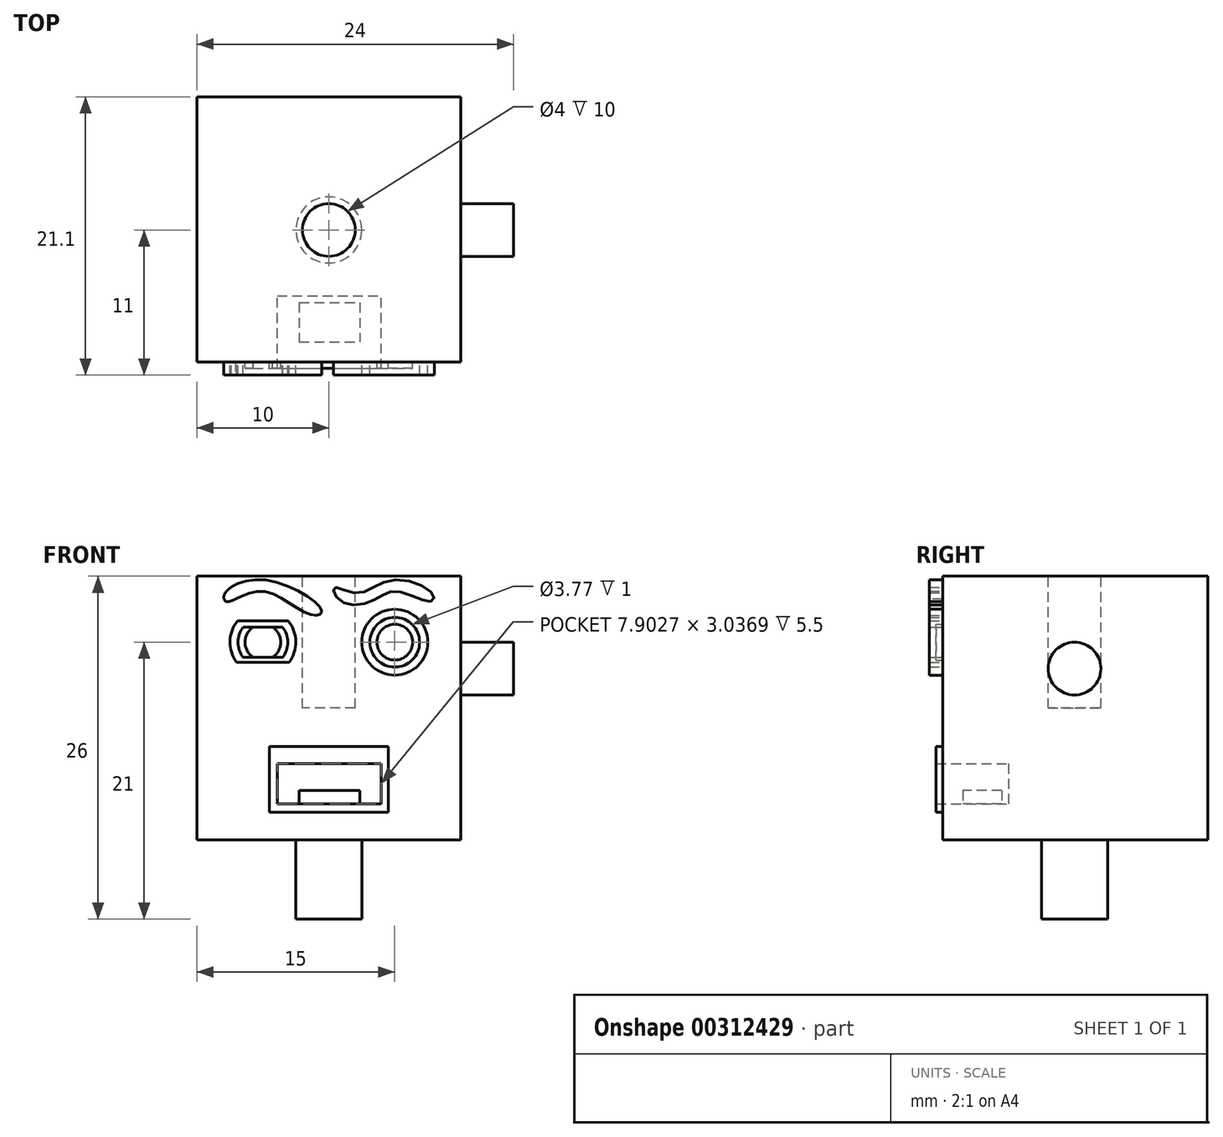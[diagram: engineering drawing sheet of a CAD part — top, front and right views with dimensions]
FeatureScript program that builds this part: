
annotation { "Feature Type Name" : "Feature", "Feature Type Description" : "" }
export const myFeature = defineFeature(function(context is Context, id is Id, definition is map)
    precondition{}
    {
        {
            var Q0;
            Q0=qCreatedBy(makeId("Front.planeOp"),FACE);
            var sketch = newSketch(context, id + "F0", { "sketchPlane" : qUnion([Q0])});
            skLineSegment(sketch, "E0.bottom", {"start": v(-10, 10) * mm, "end": v(10, 10) * mm});
            skLineSegment(sketch, "E0.top", {"start": v(-10, -10) * mm, "end": v(10, -10) * mm});
            skLineSegment(sketch, "E0.left", {"start": v(-10, 10) * mm, "end": v(-10, -10) * mm});
            skLineSegment(sketch, "E0.right", {"start": v(10, 10) * mm, "end": v(10, -10) * mm});
            skLineSegment(sketch, "E1", {"start": v(0, 10) * mm, "end": v(0, -10) * mm, "construction": true});
            skSolve(sketch);
        }
        {
            var Q0;
            Q0 = qSketchRegion(id + "F0", true);
            extrude(context, id + "F1", {"entities" : qUnion([Q0]), "depth" : 10 * mm, "hasSecondDirection" : true, "secondDirectionOppositeDirection" : true, "secondDirectionDepth" : 10.1 * mm});
        }
        {
            var Q0;
            Q0=makeQuery(id+"F1.opExtrude","CAP_FACE",FACE,{"disambiguationData":[OSD([sQuery(id+"F0.wireOp",EDGE,"E0.bottom"),sQuery(id+"F0.wireOp",EDGE,"E0.top"),sQuery(id+"F0.wireOp",EDGE,"E0.left"),sQuery(id+"F0.wireOp",EDGE,"E0.right")])],"isStart":false});
            var sketch = newSketch(context, id + "F2", { "sketchPlane" : qUnion([Q0])});
            skLineSegment(sketch, "E2", {"start": v(0, 10) * mm, "end": v(0, -10) * mm, "construction": true});
            skCircle(sketch, "E3.MirrorC", {"center": v(5, 5) * mm, "radius": 2.5 * mm});
            skCircle(sketch, "E4.MirrorC", {"center": v(5, 5) * mm, "radius": 1.88 * mm});
            skLineSegment(sketch, "E5", {"start": v(-6.97, 3.46) * mm, "end": v(-6.97, 3.46) * mm});
            skLineSegment(sketch, "E6", {"start": v(-6.91, 6.61) * mm, "end": v(-5.97, 6.61) * mm});
            skArc(sketch, "E7", {"start": v(-6.91, 6.61) * mm, "mid": v(-7.5, 5.05) * mm, "end": v(-6.97, 3.46) * mm});
            skLineSegment(sketch, "E8", {"start": v(-6.97, 3.46) * mm, "end": v(-6.1, 3.46) * mm});
            skArc(sketch, "E9", {"start": v(-3.03, 3.46) * mm, "mid": v(-2.5, 5.05) * mm, "end": v(-3.09, 6.61) * mm});
            skLineSegment(sketch, "E10", {"start": v(-5.97, 6.61) * mm, "end": v(-5.97, 6.61) * mm});
            skLineSegment(sketch, "E11", {"start": v(-4.03, 6.61) * mm, "end": v(-3.09, 6.61) * mm});
            skLineSegment(sketch, "E12", {"start": v(-3.9, 3.46) * mm, "end": v(-3.9, 3.46) * mm});
            skLineSegment(sketch, "E13", {"start": v(-6.1, 3.46) * mm, "end": v(-3.9, 3.46) * mm});
            skLineSegment(sketch, "E14", {"start": v(-5.97, 6.61) * mm, "end": v(-4.03, 6.61) * mm});
            skLineSegment(sketch, "E15", {"start": v(-6.1, 3.46) * mm, "end": v(-6.1, 3.46) * mm});
            skLineSegment(sketch, "E16", {"start": v(-3.9, 3.46) * mm, "end": v(-3.03, 3.46) * mm});
            skLineSegment(sketch, "E17", {"start": v(-6.5, 6.15) * mm, "end": v(-3.5, 6.15) * mm});
            skLineSegment(sketch, "E18", {"start": v(-6.5, 3.86) * mm, "end": v(-6.5, 3.86) * mm});
            skArc(sketch, "E19", {"start": v(-6.5, 6.15) * mm, "mid": v(-6.88, 5) * mm, "end": v(-6.5, 3.86) * mm});
            skArc(sketch, "E20", {"start": v(-3.5, 3.86) * mm, "mid": v(-3.12, 5) * mm, "end": v(-3.5, 6.15) * mm});
            skLineSegment(sketch, "E21", {"start": v(-6.5, 3.86) * mm, "end": v(-3.5, 3.86) * mm});
            skSolve(sketch);
        }
        {
            var Q0;
            Q0=makeQuery(id+"F1.opExtrude","SWEPT_FACE",FACE,{"disambiguationData":[OSD([sQuery(id+"F0.wireOp",EDGE,"E0.top")])]});
            var sketch = newSketch(context, id + "F3", { "sketchPlane" : qUnion([Q0])});
            skCircle(sketch, "E22", {"center": v(0, 0) * mm, "radius": 2.5 * mm});
            skSolve(sketch);
        }
        {
            var Q0;
            Q0 = qSketchRegion(id + "F3", true);
            extrude(context, id + "F4", {"entities" : qUnion([Q0]), "operationType" : NewBodyOperationType.ADD, "depth" : 6 * mm});
        }
        {
            var Q0;
            Q0=makeQuery(id+"F1.opExtrude","SWEPT_FACE",FACE,{"disambiguationData":[OSD([sQuery(id+"F0.wireOp",EDGE,"E0.right")])]});
            var sketch = newSketch(context, id + "F5", { "sketchPlane" : qUnion([Q0])});
            skCircle(sketch, "E23", {"center": v(0, 3) * mm, "radius": 2 * mm});
            skSolve(sketch);
        }
        {
            var Q0;
            Q0 = qSketchRegion(id + "F5", true);
            extrude(context, id + "F6", {"entities" : qUnion([Q0]), "operationType" : NewBodyOperationType.ADD, "depth" : 4 * mm});
        }
        {
            var Q0;
            Q0=makeQuery(id+"F1.opExtrude","CAP_FACE",FACE,{"disambiguationData":[OSD([sQuery(id+"F0.wireOp",EDGE,"E0.bottom"),sQuery(id+"F0.wireOp",EDGE,"E0.top"),sQuery(id+"F0.wireOp",EDGE,"E0.left"),sQuery(id+"F0.wireOp",EDGE,"E0.right")])],"isStart":false});
            var sketch = newSketch(context, id + "F7", { "sketchPlane" : qUnion([Q0])});
            skFitSpline(sketch, "E24.MirrorC", {"points": [v(7.73, 8.08) * mm, v(5.16, 8.87) * mm, v(3.2, 8.1) * mm, v(0.85, 8.15) * mm, v(0.4, 9.12) * mm, v(2.13, 8.73) * mm, v(4.82, 9.72) * mm, v(7.93, 8.59) * mm, v(7.73, 8.08) * mm]});
            skLineSegment(sketch, "E25", {"start": v(-7.22, 9.28) * mm, "end": v(-7.4, 8.13) * mm});
            skLineSegment(sketch, "E26", {"start": v(-6.92, 9.43) * mm, "end": v(-6.92, 9.43) * mm});
            skLineSegment(sketch, "E27", {"start": v(-6.92, 9.43) * mm, "end": v(-7.09, 8.26) * mm});
            skFitSpline(sketch, "E28", {"points": [v(-7.73, 8.08) * mm, v(-5.16, 8.87) * mm, v(-1.37, 7.08) * mm, v(-0.55, 7.36) * mm, v(-4.82, 9.72) * mm, v(-7.93, 8.59) * mm, v(-7.73, 8.08) * mm]});
            skLineSegment(sketch, "E29", {"start": v(-7.09, 8.26) * mm, "end": v(-7.09, 8.26) * mm});
            skSolve(sketch);
        }
        {
            var Q0;
            Q0 = qSketchRegion(id + "F7", true);
            extrude(context, id + "F8", {"entities" : qUnion([Q0]), "operationType" : NewBodyOperationType.ADD, "depth" : 1 * mm});
        }
        {
            var Q0;
            Q0 = qSketchRegion(id + "F2", true);
            extrude(context, id + "F9", {"entities" : qUnion([Q0]), "operationType" : NewBodyOperationType.ADD, "depth" : 1 * mm});
        }
        {
            var Q0;
            Q0=makeQuery(id+"F9.boolean.opBoolean","SPLIT",FACE,{"disambiguationData":[TD([makeQuery(id+"F9.opExtrude","SWEPT_FACE",FACE,{"disambiguationData":[OSD([sQuery(id+"F2.wireOp",EDGE,"E4.MirrorC")])]})])],"derivedFrom":makeQuery(id+"F1.opExtrude","CAP_FACE",FACE,{"disambiguationData":[OSD([sQuery(id+"F0.wireOp",EDGE,"E0.bottom"),sQuery(id+"F0.wireOp",EDGE,"E0.top"),sQuery(id+"F0.wireOp",EDGE,"E0.left"),sQuery(id+"F0.wireOp",EDGE,"E0.right")])],"isStart":false})});
            var sketch = newSketch(context, id + "F10", { "sketchPlane" : qUnion([Q0])});
            skCircle(sketch, "E30", {"center": v(5, 5) * mm, "radius": 1.36 * mm});
            skLineSegment(sketch, "E31", {"start": v(0, 7.57) * mm, "end": v(0, -2.24) * mm, "construction": true});
            skCircle(sketch, "E32.MirrorC", {"center": v(-5, 5) * mm, "radius": 1.36 * mm});
            skSolve(sketch);
        }
        {
            var Q0;
            Q0 = qSketchRegion(id + "F10", true);
            extrude(context, id + "F11", {"entities" : qUnion([Q0]), "operationType" : NewBodyOperationType.ADD, "depth" : 0.5 * mm});
        }
        {
            var Q0;
            {var subQ0=sQuery(id+"F0.wireOp",EDGE,"E0.bottom");var subQ1=sQuery(id+"F0.wireOp",EDGE,"E0.right");var subQ2=sQuery(id+"F0.wireOp",EDGE,"E0.top");var subQ3=sQuery(id+"F0.wireOp",EDGE,"E0.left");Q0=makeQuery(id+"F9.boolean.opBoolean","SPLIT",FACE,{"disambiguationData":[TD([makeQuery(id+"F1.opExtrude","SWEPT_FACE",FACE,{"disambiguationData":[OSD([subQ0])]})])],"derivedFrom":makeQuery(id+"F1.opExtrude","CAP_FACE",FACE,{"disambiguationData":[OSD([subQ0,subQ2,subQ3,subQ1])],"isStart":false})});}
            var sketch = newSketch(context, id + "F12", { "sketchPlane" : qUnion([Q0])});
            skLineSegment(sketch, "E33.bottom", {"start": v(-4.5, -2.9) * mm, "end": v(4.5, -2.9) * mm});
            skLineSegment(sketch, "E33.top", {"start": v(-4.5, -7.9) * mm, "end": v(4.5, -7.9) * mm});
            skLineSegment(sketch, "E33.left", {"start": v(-4.5, -2.9) * mm, "end": v(-4.5, -7.9) * mm});
            skLineSegment(sketch, "E33.right", {"start": v(4.5, -2.9) * mm, "end": v(4.5, -7.9) * mm});
            skLineSegment(sketch, "E34.bottom", {"start": v(-3.92, -4.2) * mm, "end": v(3.98, -4.2) * mm});
            skLineSegment(sketch, "E34.top", {"start": v(-3.92, -7.25) * mm, "end": v(3.98, -7.25) * mm});
            skLineSegment(sketch, "E34.left", {"start": v(-3.92, -4.2) * mm, "end": v(-3.92, -7.25) * mm});
            skLineSegment(sketch, "E34.right", {"start": v(3.98, -4.2) * mm, "end": v(3.98, -7.25) * mm});
            skSolve(sketch);
        }
        {
            var Q0;
            Q0 = qSketchRegion(id + "F12", true);
            extrude(context, id + "F13", {"entities" : qUnion([Q0]), "operationType" : NewBodyOperationType.ADD, "depth" : 0.5 * mm});
        }
        {
            var Q0;
            {var subQ0=sQuery(id+"F0.wireOp",EDGE,"E0.bottom");var subQ1=sQuery(id+"F0.wireOp",EDGE,"E0.right");var subQ2=sQuery(id+"F0.wireOp",EDGE,"E0.top");var subQ3=sQuery(id+"F0.wireOp",EDGE,"E0.left");Q0=makeQuery(id+"F13.boolean.opBoolean","SPLIT",FACE,{"disambiguationData":[TD([makeQuery(id+"F13.opExtrude","SWEPT_FACE",FACE,{"disambiguationData":[OSD([sQuery(id+"F12.wireOp",EDGE,"E34.bottom")])]})])],"derivedFrom":makeQuery(id+"F9.boolean.opBoolean","SPLIT",FACE,{"disambiguationData":[TD([makeQuery(id+"F1.opExtrude","SWEPT_FACE",FACE,{"disambiguationData":[OSD([subQ0])]})])],"derivedFrom":makeQuery(id+"F1.opExtrude","CAP_FACE",FACE,{"disambiguationData":[OSD([subQ0,subQ2,subQ3,subQ1])],"isStart":false})})});}
            extrude(context, id + "F14", {"entities" : qUnion([Q0]), "operationType" : NewBodyOperationType.REMOVE, "oppositeDirection" : true, "depth" : 5 * mm});
        }
        {
            var Q0;
            {var subQ0=sQuery(id+"F12.wireOp",EDGE,"E34.top");Q0=makeQuery(id+"F14.boolean.opBoolean","MERGE",FACE,{"derivedFrom":[makeQuery(id+"F13.opExtrude","SWEPT_FACE",FACE,{"disambiguationData":[OSD([subQ0])]}),makeQuery(id+"F14.opExtrude","SWEPT_FACE",FACE,{"disambiguationData":[OSD([subQ0])]})]});}
            var sketch = newSketch(context, id + "F15", { "sketchPlane" : qUnion([Q0])});
            skLineSegment(sketch, "E35.bottom", {"start": v(-2.24, -5.52) * mm, "end": v(2.35, -5.52) * mm});
            skLineSegment(sketch, "E35.top", {"start": v(-2.24, -8.48) * mm, "end": v(2.35, -8.48) * mm});
            skLineSegment(sketch, "E35.left", {"start": v(-2.24, -5.52) * mm, "end": v(-2.24, -8.48) * mm});
            skLineSegment(sketch, "E35.right", {"start": v(2.35, -5.52) * mm, "end": v(2.35, -8.48) * mm});
            skSolve(sketch);
        }
        {
            var Q0;
            Q0 = qSketchRegion(id + "F15", true);
            extrude(context, id + "F16", {"entities" : qUnion([Q0]), "operationType" : NewBodyOperationType.ADD, "depth" : 1 * mm});
        }
        {
            var Q0;
            Q0=makeQuery(id+"F1.opExtrude","SWEPT_FACE",FACE,{"disambiguationData":[OSD([sQuery(id+"F0.wireOp",EDGE,"E0.bottom")])]});
            var sketch = newSketch(context, id + "F17", { "sketchPlane" : qUnion([Q0])});
            skCircle(sketch, "E36", {"center": v(0, 0) * mm, "radius": 2 * mm});
            skSolve(sketch);
        }
        {
            var Q0;
            Q0 = qSketchRegion(id + "F17", true);
            extrude(context, id + "F18", {"entities" : qUnion([Q0]), "operationType" : NewBodyOperationType.REMOVE, "oppositeDirection" : true, "depth" : 10 * mm});
        }
    });
